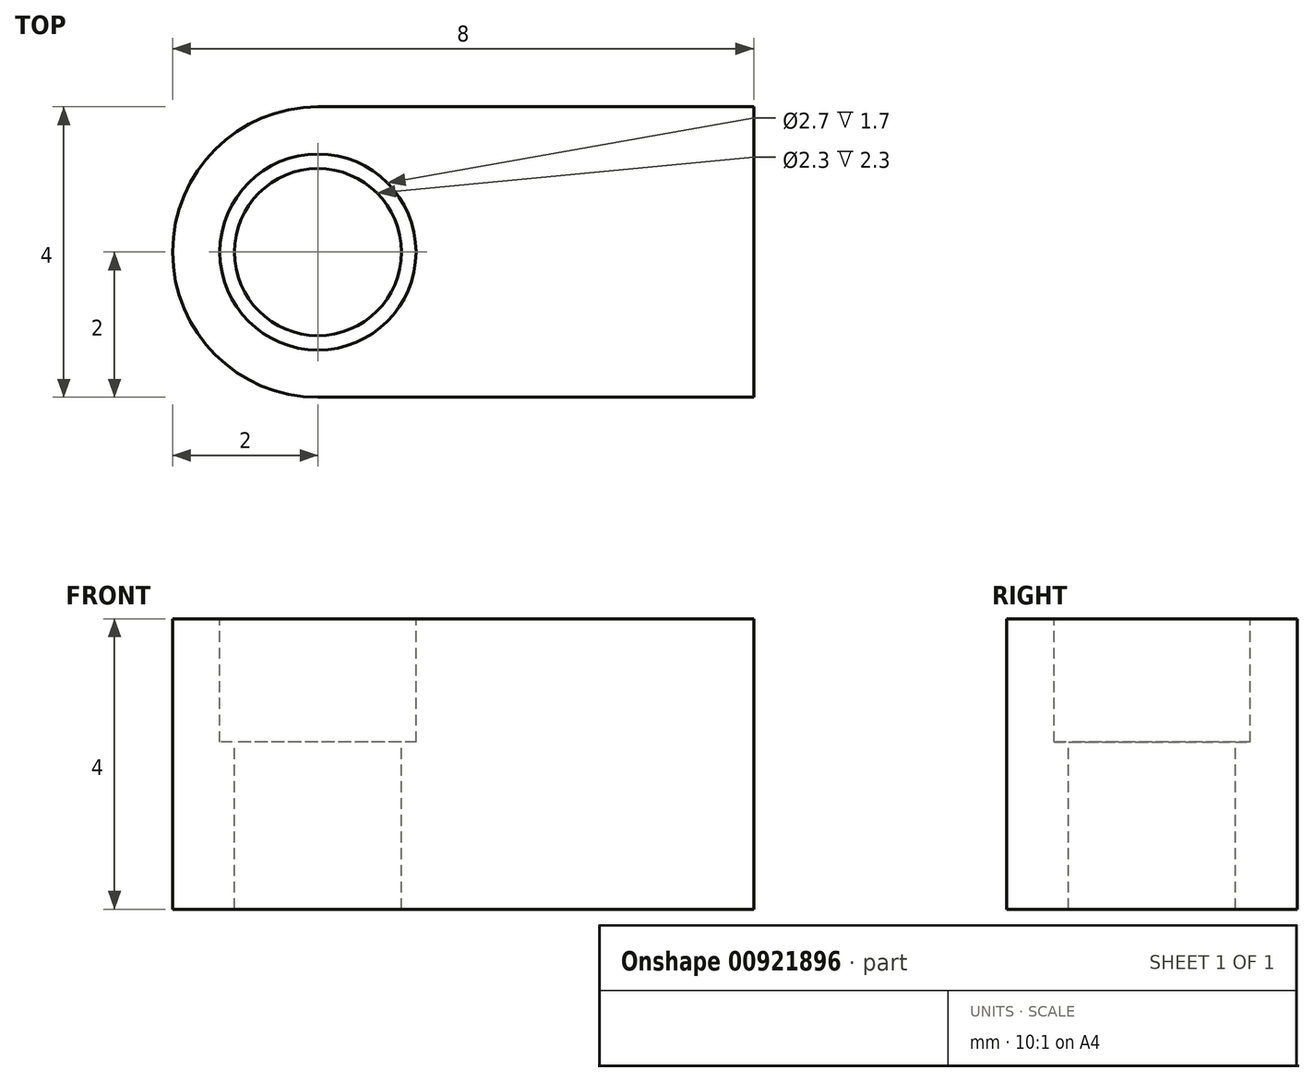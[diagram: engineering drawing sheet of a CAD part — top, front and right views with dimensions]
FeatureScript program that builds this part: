
annotation { "Feature Type Name" : "Feature", "Feature Type Description" : "" }
export const myFeature = defineFeature(function(context is Context, id is Id, definition is map)
    precondition{}
    {
        {
            var Q0;
            Q0=qCreatedBy(makeId("Top.planeOp"),FACE);
            var sketch = newSketch(context, id + "F0", { "sketchPlane" : qUnion([Q0])});
            skLineSegment(sketch, "E0.bottom", {"start": v(0, 0) * mm, "end": v(6, 0) * mm});
            skLineSegment(sketch, "E0.top", {"start": v(0, 4) * mm, "end": v(6, 4) * mm});
            skLineSegment(sketch, "E0.left", {"start": v(0, 0) * mm, "end": v(0, 4) * mm});
            skLineSegment(sketch, "E0.right", {"start": v(6, 0) * mm, "end": v(6, 4) * mm});
            skCircle(sketch, "E1", {"center": v(0, 2) * mm, "radius": 2 * mm});
            skSolve(sketch);
        }
        {
            var Q0;
            {var subQ0=sQuery(id+"F0.wireOp",EDGE,"E0.left");Q0=makeQuery(id+"F0.imprint","IMPRINT",FACE,{"disambiguationData":[TD([[makeQuery(id+"F0.imprint","IMPRINT",EDGE,{"derivedFrom":subQ0}),1.0]])]});}
            var Q1;
            {var subQ0=sQuery(id+"F0.wireOp",EDGE,"E0.left");Q1=makeQuery(id+"F0.imprint","IMPRINT",FACE,{"disambiguationData":[TD([[makeQuery(id+"F0.imprint","IMPRINT",EDGE,{"derivedFrom":subQ0}),-1.0]])]});}
            var Q2;
            {var subQ0=sQuery(id+"F0.wireOp",EDGE,"E0.bottom");Q2=makeQuery(id+"F0.imprint","IMPRINT",FACE,{"disambiguationData":[TD([[makeQuery(id+"F0.imprint","IMPRINT",EDGE,{"derivedFrom":subQ0}),1.0]])]});}
            extrude(context, id + "F1", {"entities" : qUnion([Q0, Q1, Q2]), "depth" : 4 * mm, "offsetDistance" : 25 * mm});
        }
        {
            var Q0;
            Q0=makeQuery(id+"F1.opExtrude","CAP_FACE",FACE,{"disambiguationData":[OSD([sQuery(id+"F0.wireOp",EDGE,"E0.bottom"),sQuery(id+"F0.wireOp",EDGE,"E0.top"),sQuery(id+"F0.wireOp",EDGE,"E0.right"),sQuery(id+"F0.wireOp",EDGE,"E1")])],"isStart":false});
            var sketch = newSketch(context, id + "F2", { "sketchPlane" : qUnion([Q0])});
            skCircle(sketch, "E2", {"center": v(0, 2) * mm, "radius": 1.35 * mm});
            skSolve(sketch);
        }
        {
            var Q0;
            Q0=makeQuery(id+"F2.imprint","IMPRINT",FACE,{"disambiguationData":[TD([[makeQuery(id+"F2.imprint","IMPRINT",EDGE,{"derivedFrom":sQuery(id+"F2.wireOp",EDGE,"E2")}),1.0]])]});
            extrude(context, id + "F3", {"entities" : qUnion([Q0]), "operationType" : NewBodyOperationType.REMOVE, "oppositeDirection" : true, "depth" : 1.7 * mm, "offsetDistance" : 25 * mm});
        }
        {
            var Q0;
            Q0=makeQuery(id+"F3.boolean.opBoolean","COPY",FACE,{"derivedFrom":makeQuery(id+"F3.opExtrude","CAP_FACE",FACE,{"disambiguationData":[OSD([sQuery(id+"F2.wireOp",EDGE,"E2")])],"isStart":false})});
            var sketch = newSketch(context, id + "F4", { "sketchPlane" : qUnion([Q0])});
            skCircle(sketch, "E3", {"center": v(0, 2) * mm, "radius": 1.15 * mm});
            skSolve(sketch);
        }
        {
            var Q0;
            Q0=makeQuery(id+"F4.imprint","IMPRINT",FACE,{"disambiguationData":[TD([[makeQuery(id+"F4.imprint","IMPRINT",EDGE,{"derivedFrom":sQuery(id+"F4.wireOp",EDGE,"E3")}),1.0]])]});
            extrude(context, id + "F5", {"entities" : qUnion([Q0]), "operationType" : NewBodyOperationType.REMOVE, "oppositeDirection" : true, "depth" : 4 * mm, "offsetDistance" : 25 * mm});
        }
    });
